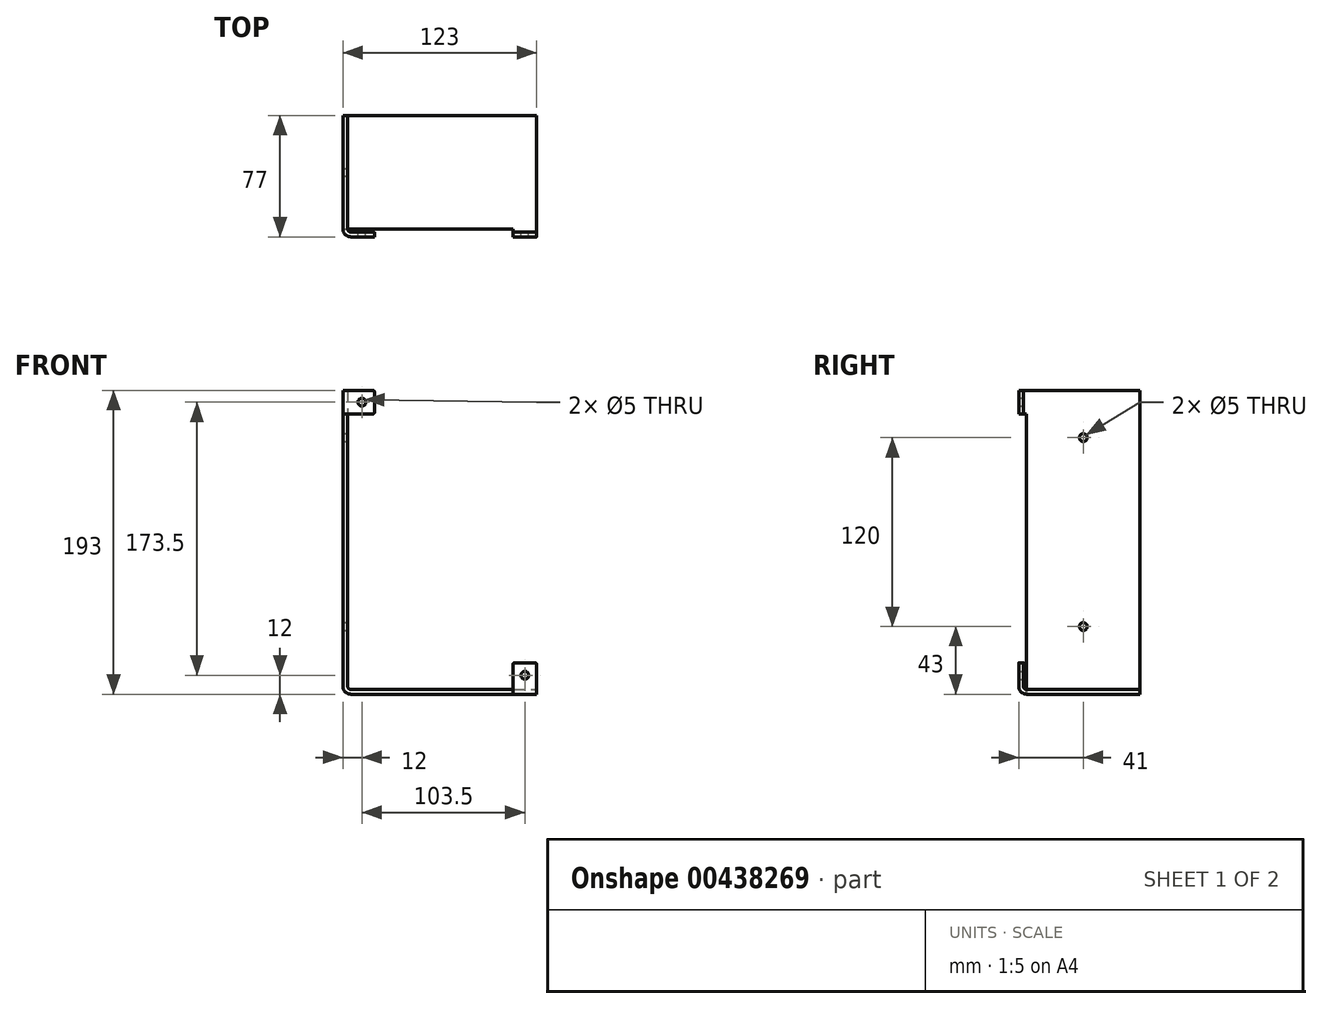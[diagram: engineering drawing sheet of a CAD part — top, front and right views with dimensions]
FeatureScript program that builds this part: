
annotation { "Feature Type Name" : "Feature", "Feature Type Description" : "" }
export const myFeature = defineFeature(function(context is Context, id is Id, definition is map)
    precondition{}
    {
        {
            var Q0;
            Q0=qCreatedBy(makeId("Front.planeOp"),FACE);
            var sketch = newSketch(context, id + "F0", { "sketchPlane" : qUnion([Q0])});
            skLineSegment(sketch, "E0", {"start": v(0, 190) * mm, "end": v(0, 2) * mm});
            skLineSegment(sketch, "E1", {"start": v(2, 0) * mm, "end": v(120, 0) * mm});
            skPoint(sketch, "E2.visualSharp", {"position": v(0, 0) * mm});
            skArc(sketch, "E2.filletArc", {"start": v(0, 2) * mm, "mid": v(0.59, 0.59) * mm, "end": v(2, 0) * mm});
            skLineSegment(sketch, "E3.0", {"start": v(2, -3) * mm, "end": v(120, -3) * mm});
            skArc(sketch, "E3.1", {"start": v(-3, 2) * mm, "mid": v(-1.54, -1.54) * mm, "end": v(2, -3) * mm});
            skLineSegment(sketch, "E3.2", {"start": v(-3, 190) * mm, "end": v(-3, 2) * mm});
            skLineSegment(sketch, "E4", {"start": v(120, -3) * mm, "end": v(120, 0) * mm});
            skLineSegment(sketch, "E5", {"start": v(-3, 190) * mm, "end": v(0, 190) * mm});
            skSolve(sketch);
        }
        {
            var Q0;
            Q0 = qSketchRegion(id + "F0", true);
            extrude(context, id + "F1", {"entities" : qUnion([Q0]), "depth" : 72 * mm});
        }
        {
            var Q0;
            Q0=makeQuery(id+"F1.opExtrude","SWEPT_FACE",FACE,{"disambiguationData":[OSD([sQuery(id+"F0.wireOp",EDGE,"E5")])]});
            var sketch = newSketch(context, id + "F2", { "sketchPlane" : qUnion([Q0])});
            skArc(sketch, "E6", {"start": v(0, -72) * mm, "mid": v(0.59, -73.41) * mm, "end": v(2, -74) * mm});
            skLineSegment(sketch, "E7", {"start": v(2, -74) * mm, "end": v(17, -74) * mm});
            skLineSegment(sketch, "E8", {"start": v(0, -72) * mm, "end": v(-3, -72) * mm});
            skLineSegment(sketch, "E9.0", {"start": v(2, -77) * mm, "end": v(17, -77) * mm});
            skArc(sketch, "E9.1", {"start": v(-3, -72) * mm, "mid": v(-1.54, -75.54) * mm, "end": v(2, -77) * mm});
            skLineSegment(sketch, "E10", {"start": v(17, -77) * mm, "end": v(17, -74) * mm});
            skSolve(sketch);
        }
        {
            var Q0;
            Q0 = qSketchRegion(id + "F2", true);
            extrude(context, id + "F3", {"entities" : qUnion([Q0]), "operationType" : NewBodyOperationType.ADD, "oppositeDirection" : true, "depth" : 15 * mm});
        }
        {
            var Q0;
            Q0=makeQuery(id+"F1.opExtrude","SWEPT_FACE",FACE,{"disambiguationData":[OSD([sQuery(id+"F0.wireOp",EDGE,"E4")])]});
            var sketch = newSketch(context, id + "F4", { "sketchPlane" : qUnion([Q0])});
            skArc(sketch, "E11", {"start": v(-74, 2) * mm, "mid": v(-73.41, 0.59) * mm, "end": v(-72, 0) * mm});
            skLineSegment(sketch, "E12", {"start": v(-74, 2) * mm, "end": v(-74, 17) * mm});
            skLineSegment(sketch, "E13", {"start": v(-72, 0) * mm, "end": v(-72, -3) * mm});
            skLineSegment(sketch, "E14.0", {"start": v(-77, 2) * mm, "end": v(-77, 17) * mm});
            skArc(sketch, "E14.1", {"start": v(-77, 2) * mm, "mid": v(-75.54, -1.54) * mm, "end": v(-72, -3) * mm});
            skLineSegment(sketch, "E15", {"start": v(-77, 17) * mm, "end": v(-74, 17) * mm});
            skSolve(sketch);
        }
        {
            var Q0;
            Q0 = qSketchRegion(id + "F4", true);
            extrude(context, id + "F5", {"entities" : qUnion([Q0]), "operationType" : NewBodyOperationType.ADD, "oppositeDirection" : true, "depth" : 15 * mm});
        }
        {
            var Q0;
            Q0=makeQuery(id+"F5.opExtrude","CAP_EDGE",EDGE,{"disambiguationData":[OSD([sQuery(id+"F4.wireOp",EDGE,"E15")])],"isStart":true});
            var Q1;
            Q1=makeQuery(id+"F5.opExtrude","CAP_EDGE",EDGE,{"disambiguationData":[OSD([sQuery(id+"F4.wireOp",EDGE,"E15")])],"isStart":false});
            var Q2;
            Q2=makeQuery(id+"F3.opExtrude","CAP_EDGE",EDGE,{"disambiguationData":[OSD([sQuery(id+"F2.wireOp",EDGE,"E10")])],"isStart":true});
            var Q3;
            Q3=makeQuery(id+"F3.opExtrude","CAP_EDGE",EDGE,{"disambiguationData":[OSD([sQuery(id+"F2.wireOp",EDGE,"E10")])],"isStart":false});
            fillet(context, id + "F6", {"entities" : qUnion([Q0, Q1, Q2, Q3]), "radius" : 1 * mm, "tangentPropagation" : true, "allowEdgeOverflow" : false});
        }
        {
            var Q0;
            Q0=makeQuery(id+"F5.opExtrude","SWEPT_FACE",FACE,{"disambiguationData":[OSD([sQuery(id+"F4.wireOp",EDGE,"E14.0")])]});
            var sketch = newSketch(context, id + "F7", { "sketchPlane" : qUnion([Q0])});
            skPoint(sketch, "E16", {"position": v(112.5, 9) * mm});
            skPoint(sketch, "E16.positionSnap0", {"position": v(120, 9) * mm});
            skPoint(sketch, "E16.positionSnap1", {"position": v(112.5, 17) * mm});
            skSolve(sketch);
        }
        {
            var Q0;
            Q0=makeQuery(id+"F3.opExtrude","SWEPT_FACE",FACE,{"disambiguationData":[OSD([sQuery(id+"F2.wireOp",EDGE,"E9.0")])]});
            var sketch = newSketch(context, id + "F8", { "sketchPlane" : qUnion([Q0])});
            skPoint(sketch, "E17", {"position": v(9, 182.5) * mm});
            skPoint(sketch, "E17.positionSnap0", {"position": v(17, 182.5) * mm});
            skPoint(sketch, "E17.positionSnap1", {"position": v(9, 190) * mm});
            skSolve(sketch);
        }
        {
            var Q0;
            Q0=sQuery(id+"F8.wireOp",VERTEX,"E17");
            var Q1;
            Q1=sQuery(id+"F7.wireOp",VERTEX,"E16");
            var Q2;
            Q2=makeQuery(id+"F1.opExtrude","SWEPT_BODY",BODY,{"disambiguationData":[OSD([sQuery(id+"F0.wireOp",EDGE,"E0"),sQuery(id+"F0.wireOp",EDGE,"E1"),sQuery(id+"F0.wireOp",EDGE,"E2.filletArc"),sQuery(id+"F0.wireOp",EDGE,"E3.0"),sQuery(id+"F0.wireOp",EDGE,"E3.1"),sQuery(id+"F0.wireOp",EDGE,"E3.2"),sQuery(id+"F0.wireOp",EDGE,"E4"),sQuery(id+"F0.wireOp",EDGE,"E5")])]});
            hole(context, id + "F9", {"style" : HoleStyle.SIMPLE, "endStyle" : HoleEndStyle.THROUGH, "holeDiameter" : 5 * mm, "isTappedThrough" : true, "tappedDepth" : 12 * mm, "tapClearance" : 3, "locations" : qUnion([Q0, Q1]), "scope" : qUnion([Q2]), "startStyle" : HoleStartStyle.PART});
        }
        {
            var Q0;
            Q0=makeQuery(id+"F1.opExtrude","SWEPT_FACE",FACE,{"disambiguationData":[OSD([sQuery(id+"F0.wireOp",EDGE,"E3.2")])]});
            var sketch = newSketch(context, id + "F10", { "sketchPlane" : qUnion([Q0])});
            skPoint(sketch, "E18", {"position": v(36, 160) * mm});
            skPoint(sketch, "E18.positionSnap0", {"position": v(36, 190) * mm});
            skPoint(sketch, "E19", {"position": v(36, 40) * mm});
            skSolve(sketch);
        }
        {
            var Q0;
            Q0=sQuery(id+"F10.wireOp",VERTEX,"E18");
            var Q1;
            Q1=sQuery(id+"F10.wireOp",VERTEX,"E19");
            var Q2;
            Q2=makeQuery(id+"F1.opExtrude","SWEPT_BODY",BODY,{"disambiguationData":[OSD([sQuery(id+"F0.wireOp",EDGE,"E0"),sQuery(id+"F0.wireOp",EDGE,"E1"),sQuery(id+"F0.wireOp",EDGE,"E2.filletArc"),sQuery(id+"F0.wireOp",EDGE,"E3.0"),sQuery(id+"F0.wireOp",EDGE,"E3.1"),sQuery(id+"F0.wireOp",EDGE,"E3.2"),sQuery(id+"F0.wireOp",EDGE,"E4"),sQuery(id+"F0.wireOp",EDGE,"E5")])]});
            hole(context, id + "F11", {"style" : HoleStyle.SIMPLE, "endStyle" : HoleEndStyle.THROUGH, "holeDiameter" : 5 * mm, "isTappedThrough" : true, "tappedDepth" : 12 * mm, "tapClearance" : 3, "locations" : qUnion([Q0, Q1]), "scope" : qUnion([Q2]), "startStyle" : HoleStartStyle.PART});
        }
    });
